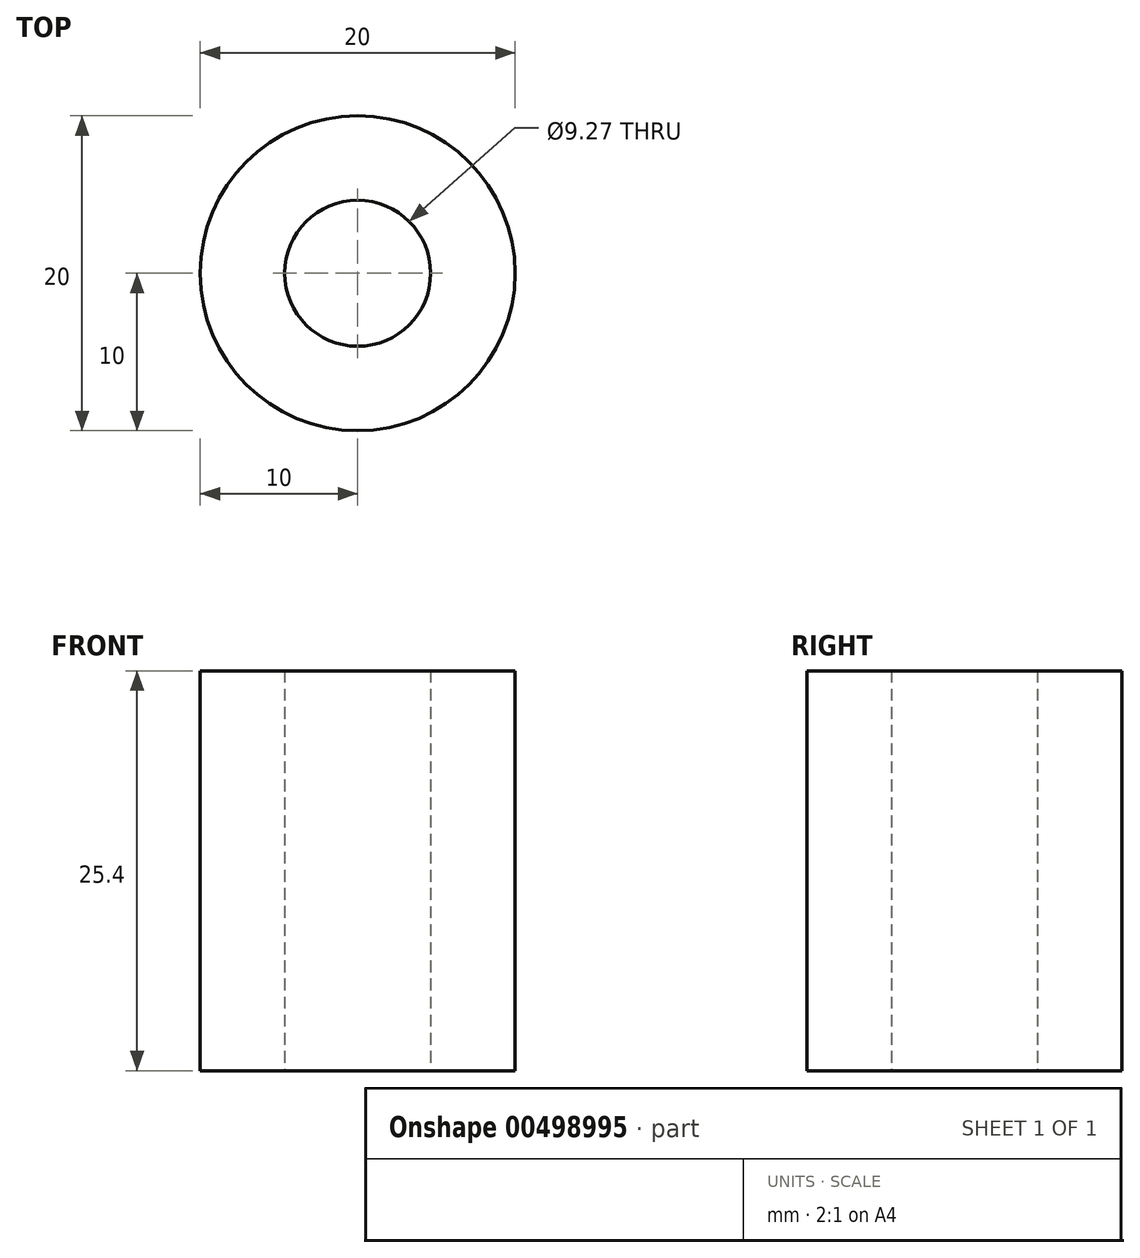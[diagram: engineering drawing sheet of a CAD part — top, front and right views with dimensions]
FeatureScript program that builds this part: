
annotation { "Feature Type Name" : "Feature", "Feature Type Description" : "" }
export const myFeature = defineFeature(function(context is Context, id is Id, definition is map)
    precondition{}
    {
        {
            var Q0;
            Q0=qCreatedBy(makeId("Top.planeOp"),FACE);
            var sketch = newSketch(context, id + "F0", { "sketchPlane" : qUnion([Q0])});
            skCircle(sketch, "E0", {"center": v(0, 0) * mm, "radius": 10 * mm});
            skCircle(sketch, "E1", {"center": v(0, 0) * mm, "radius": 4.64 * mm});
            skSolve(sketch);
        }
        {
            var Q0;
            Q0 = qSketchRegion(id + "F0", true);
            extrude(context, id + "F1", {"entities" : qUnion([Q0]), "depth" : 25.4 * mm});
        }
    });
